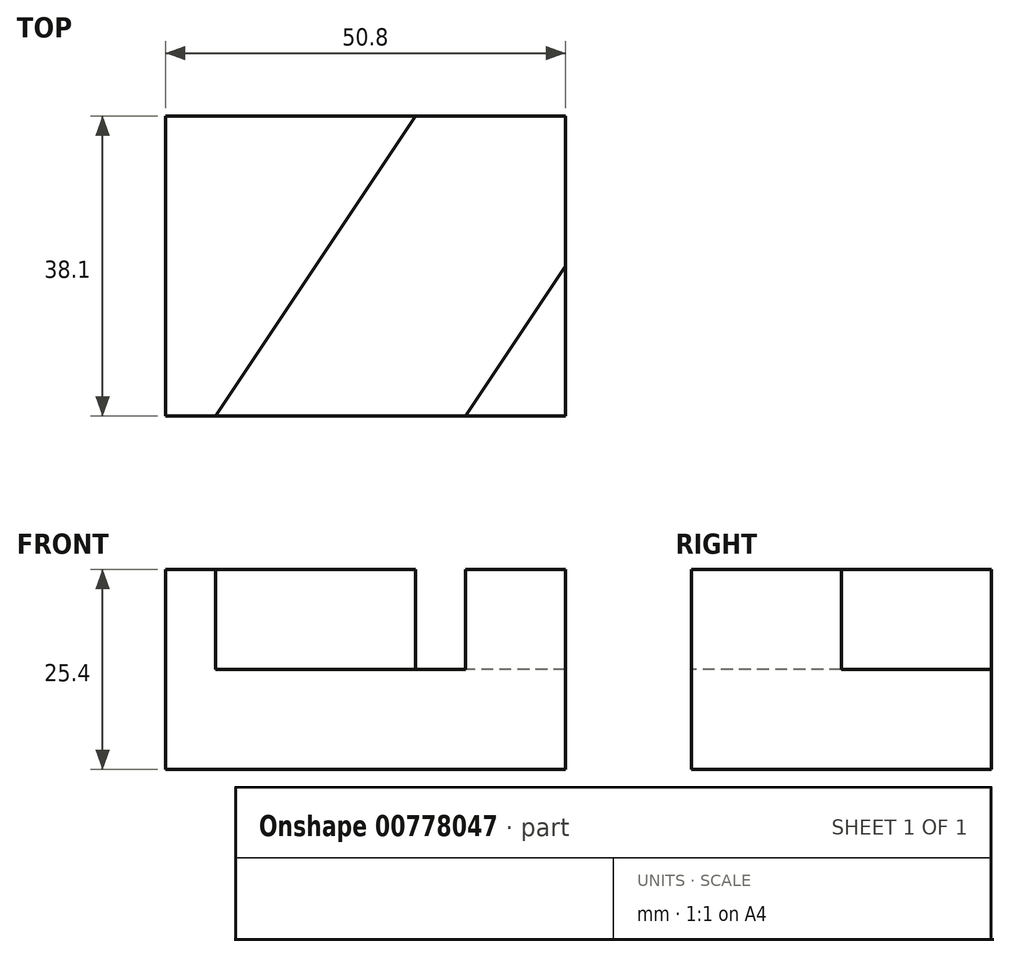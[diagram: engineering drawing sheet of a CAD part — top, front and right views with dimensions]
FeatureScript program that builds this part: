
annotation { "Feature Type Name" : "Feature", "Feature Type Description" : "" }
export const myFeature = defineFeature(function(context is Context, id is Id, definition is map)
    precondition{}
    {
        {
            var Q0;
            Q0=qCreatedBy(makeId("Front.planeOp"),FACE);
            var sketch = newSketch(context, id + "F0", { "sketchPlane" : qUnion([Q0])});
            skLineSegment(sketch, "E0", {"start": v(0, 0) * mm, "end": v(50.8, 0) * mm});
            skLineSegment(sketch, "E1", {"start": v(50.8, 0) * mm, "end": v(50.8, 25.4) * mm});
            skLineSegment(sketch, "E2", {"start": v(50.8, 25.4) * mm, "end": v(0, 25.4) * mm});
            skLineSegment(sketch, "E3", {"start": v(0, 25.4) * mm, "end": v(0, 0) * mm});
            skSolve(sketch);
        }
        {
            var Q0;
            Q0=makeQuery(id+"F0.imprint","IMPRINT",FACE,{"disambiguationData":[TD([[makeQuery(id+"F0.imprint","IMPRINT",EDGE,{"derivedFrom":sQuery(id+"F0.wireOp",EDGE,"E0")}),1.0]])]});
            extrude(context, id + "F1", {"entities" : qUnion([Q0]), "depth" : 38.1 * mm, "offsetDistance" : 25.4 * mm});
        }
        {
            var Q0;
            Q0=makeQuery(id+"F1.opExtrude","SWEPT_FACE",FACE,{"disambiguationData":[OSD([sQuery(id+"F0.wireOp",EDGE,"E2")])]});
            var sketch = newSketch(context, id + "F2", { "sketchPlane" : qUnion([Q0])});
            skLineSegment(sketch, "E4", {"start": v(0, -38.1) * mm, "end": v(6.35, -38.1) * mm});
            skLineSegment(sketch, "E5", {"start": v(0, 0) * mm, "end": v(31.75, 0) * mm});
            skLineSegment(sketch, "E6", {"start": v(31.75, 0) * mm, "end": v(6.35, -38.1) * mm});
            skSolve(sketch);
        }
        {
            var Q0;
            {var subQ0=sQuery(id+"F2.wireOp",EDGE,"E6");Q0=makeQuery(id+"F2.imprint","IMPRINT",FACE,{"disambiguationData":[TD([[makeQuery(id+"F2.imprint","IMPRINT",EDGE,{"derivedFrom":subQ0}),1.0]])]});}
            extrude(context, id + "F3", {"entities" : qUnion([Q0]), "operationType" : NewBodyOperationType.REMOVE, "oppositeDirection" : true, "depth" : 12.7 * mm, "offsetDistance" : 25.4 * mm});
        }
        {
            var Q0;
            Q0=makeQuery(id+"F3.boolean.opBoolean","COPY",FACE,{"derivedFrom":makeQuery(id+"F3.opExtrude","CAP_FACE",FACE,{"disambiguationData":[OSD([sQuery(id+"F0.wireOp",EDGE,"E1"),sQuery(id+"F0.wireOp",EDGE,"E2"),sQuery(id+"F2.wireOp",EDGE,"E6")])],"isStart":false})});
            var sketch = newSketch(context, id + "F4", { "sketchPlane" : qUnion([Q0])});
            skLineSegment(sketch, "E7", {"start": v(50.8, -38.1) * mm, "end": v(38.1, -38.1) * mm});
            skLineSegment(sketch, "E8", {"start": v(50.8, 0) * mm, "end": v(50.8, -19.05) * mm});
            skLineSegment(sketch, "E9", {"start": v(50.8, -19.05) * mm, "end": v(38.1, -38.1) * mm});
            skSolve(sketch);
        }
        {
            var Q0;
            {var subQ0=sQuery(id+"F4.wireOp",EDGE,"E7");Q0=makeQuery(id+"F4.imprint","IMPRINT",FACE,{"disambiguationData":[TD([[makeQuery(id+"F4.imprint","IMPRINT",EDGE,{"derivedFrom":subQ0}),-1.0]])]});}
            extrude(context, id + "F5", {"entities" : qUnion([Q0]), "operationType" : NewBodyOperationType.ADD, "depth" : 12.7 * mm, "offsetDistance" : 25.4 * mm});
        }
    });
